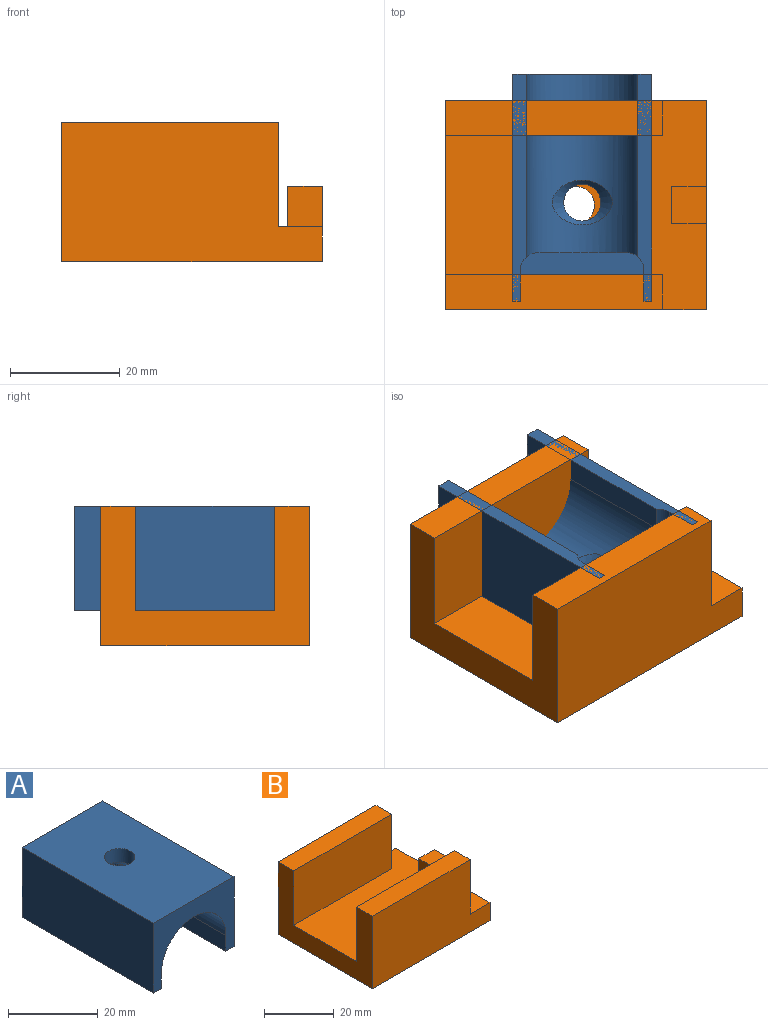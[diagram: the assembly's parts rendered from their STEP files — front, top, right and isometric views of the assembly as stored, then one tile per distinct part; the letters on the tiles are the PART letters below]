
ASSEMBLY  parts=2 mates=1
PART A: 18 faces, bbox 25.4x41.4x19.1 mm
  f0: cylinder r=10.16mm len=33.27mm, axis (0,-1,0), area 970.8mm2, adj f4,f8,f9,f10,f11,f12,f16
  f1: plane 25.4x19.05mm, normal (0,1,0), area 134.4mm2, adj f2,f3,f5,f6,f7,f13,f14,f15
  f2: plane 41.4x2.54mm, normal (0,0,-1), area 96.9mm2, adj f1,f4,f6,f8,f11,f14
  f3: plane 41.4x2.54mm, normal (0,0,-1), area 96.9mm2, adj f1,f4,f5,f9,f12,f13
  f4: plane 25.4x19.05mm, normal (0,-1,0), area 234mm2, adj f0,f2,f3,f5,f6,f7,f8,f9
  f5: plane 41.4x19.05mm, normal (1,0,0), area 788.7mm2, adj f1,f3,f4,f7
  f6: plane 41.4x19.05mm, normal (-1,0,0), area 788.7mm2, adj f1,f2,f4,f7
  f7: plane 41.4x25.4mm, normal (0,0,1), area 1015.8mm2, adj f1,f4,f5,f6,f17
  f8: plane 33.27x4.32mm, normal (1,0,0), area 143.7mm2, adj f0,f2,f4,f11
  f9: plane 33.27x4.32mm, normal (-1,0,0), area 143.7mm2, adj f0,f3,f4,f12
  f10: plane 16.21x5.05mm, normal (0,1,0), area 36.2mm2, adj f0,f11,f12,f15
  f11: cylinder r=3.17mm len=15.49mm, axis (0,0,-1), area 58.5mm2, adj f0,f2,f8,f10,f14,f15
  f12: cylinder r=3.17mm len=15.49mm, axis (0,0,-1), area 58.5mm2, adj f0,f3,f9,f10,f13,f15
  f13: plane 15.49x5.72mm, normal (-1,0,0), area 88.5mm2, adj f1,f3,f12,f15
  f14: plane 15.49x5.72mm, normal (1,0,0), area 88.5mm2, adj f1,f2,f11,f15
  f15: plane 22.56x8.89mm, normal (0,0,-1), area 196.2mm2, adj f1,f10,f11,f12,f13,f14
  f16: cone r=3.38mm half-angle=41deg, axis (0,0,-1), area 50.5mm2, adj f0,f17
  f17: cylinder r=3.38mm len=6.76mm, axis (0,0,-1), area 79.6mm2, adj f7,f16
PART B: 17 faces, bbox 47.6x38.1x25.4 mm
  f0: plane 38.1x13.72mm, normal (1,0,0), area 292.5mm2, adj f1,f2,f6,f10,f12,f14,f15
  f1: plane 47.63x25.4mm, normal (0,1,0), area 1057.3mm2, adj f0,f4,f5,f6,f13,f14
  f2: plane 47.63x25.4mm, normal (0,-1,0), area 1057.3mm2, adj f0,f3,f5,f6,f9,f14
  f3: plane 39.62x6.35mm, normal (0,0,1), area 251.6mm2, adj f2,f5,f8,f9
  f4: plane 39.62x6.35mm, normal (0,0,1), area 251.6mm2, adj f1,f5,f7,f13
  f5: plane 38.1x25.4mm, normal (-1,0,0), area 483.9mm2, adj f1,f2,f3,f4,f6,f7,f8,f14
  f6: plane 47.63x38.1mm, normal (0,0,-1), area 1778.7mm2, adj f0,f1,f2,f5,f16
  f7: plane 39.62x19.05mm, normal (0,-1,0), area 754.8mm2, adj f4,f5,f13,f14
  f8: plane 39.62x19.05mm, normal (0,1,0), area 754.8mm2, adj f3,f5,f9,f14
  f9: plane 19.05x6.35mm, normal (1,0,0), area 121mm2, adj f2,f3,f8,f14
  f10: plane 7.37x6.35mm, normal (0,-1,0), area 46.8mm2, adj f0,f11,f14,f15
  f11: plane 7.37x6.86mm, normal (-1,0,0), area 50.5mm2, adj f10,f12,f14,f15
  f12: plane 7.37x6.35mm, normal (0,1,0), area 46.8mm2, adj f0,f11,f14,f15
  f13: plane 19.05x6.35mm, normal (1,0,0), area 121mm2, adj f1,f4,f7,f14
  f14: plane 47.63x38.1mm, normal (0,0,1), area 1231.9mm2, adj f0,f1,f2,f5,f7,f8,f9,f10
  f15: plane 6.86x6.35mm, normal (0,0,1), area 43.5mm2, adj f0,f10,f11,f12
  f16: cylinder r=3.38mm len=6.76mm, axis (0,0,1), area 134.8mm2, adj f6,f14
PLACE A rot(axis=(1,0,0),180deg) t=(-14.41,15.61,30.72)mm
PLACE B t=(-15.55,12.47,24.37)mm
MATE planar A.f7 <-> B.f14  axis (0,0,-1) through (-14.41,15.71,30.72)mm
